# Revit family: Entrance-Flooring_Grate_Reese_Perfec-Grate
name_source: partatom
category: Generic Models
units: mm (PartAtom-declared; Revit-internal decimal feet)

## family parameters
Always vertical = No
Can host rebar = No
Classification Number = 23.35.50.11.24
Cut with Voids When Loaded = No
Maintain Annotation Orientation = No
Part Type = Normal
Room Calculation Point = No
Round Connector Dimension = Use Diameter
Shared = No
Work Plane-Based = Yes

## types (1)
- Recessed Mat
    Assembly Code = E1090900
    Capacity = 1000 lbs Wheel Rolling Load
    Construction Details = http://www.arcat.com
    Default Elevation = 0' - 0"
    Description = Reese Recessed Heavy Duty VariStrip Pedestrian Floor Grate - Perfec Grate as Specified
    Expected Lifespan (Years) = 0
    Keynote = 12 48 00
    Maintenance Schedule (Months) = 0
    Manufacturer = Reese Enterprises, Inc
    Manufacturer Fax = 800-334-8823 , 651-423-2662
    Manufacturer Website = http://www.reeseusa.com
    Model = Perfec Grate
    Product Data = http://www.arcat.com
    Product Properties = http://www.reeseusa.com
    Recessed Mat = Yes
    Revision = R1_2017-09
    Sales Information = http://www.reeseusa.com
    Specification = http://www.arcat.com
    Standards Conformance = as Specified
    URL = http://www.reeseusa.com
    Unit Height = 2' - 8"
    Warranty Duration (Years) = 0

## geometry (parser evidence)
native form markers: Sweep x4
no freeform markers — native parametric forms only
